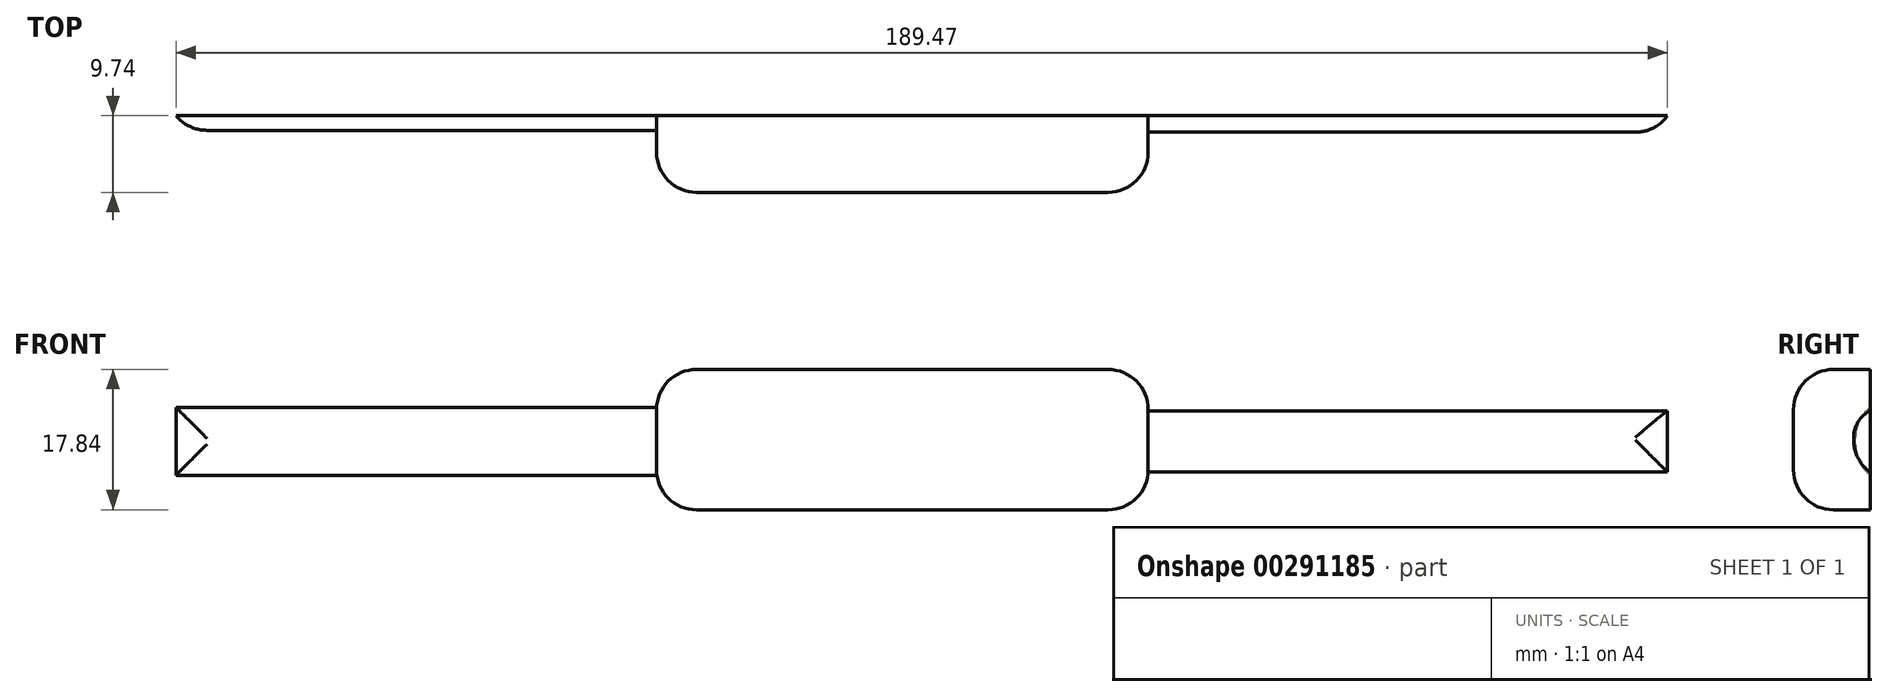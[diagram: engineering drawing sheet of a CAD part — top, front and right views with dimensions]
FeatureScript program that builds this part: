
annotation { "Feature Type Name" : "Feature", "Feature Type Description" : "" }
export const myFeature = defineFeature(function(context is Context, id is Id, definition is map)
    precondition{}
    {
        {
            var Q0;
            Q0=qCreatedBy(makeId("Front.planeOp"),FACE);
            var sketch = newSketch(context, id + "F0", { "sketchPlane" : qUnion([Q0])});
            skLineSegment(sketch, "E0.bottom", {"start": v(0, 0) * mm, "end": v(62.44, 0) * mm});
            skLineSegment(sketch, "E0.top", {"start": v(0, 17.84) * mm, "end": v(62.44, 17.84) * mm});
            skLineSegment(sketch, "E0.left", {"start": v(0, 0) * mm, "end": v(0, 17.84) * mm});
            skLineSegment(sketch, "E0.right", {"start": v(62.44, 0) * mm, "end": v(62.44, 17.84) * mm});
            skSolve(sketch);
        }
        {
            var Q0;
            Q0=makeQuery(id+"F0.imprint","IMPRINT",FACE,{"disambiguationData":[TD([[makeQuery(id+"F0.imprint","IMPRINT",EDGE,{"derivedFrom":sQuery(id+"F0.wireOp",EDGE,"E0.bottom")}),1.0]])]});
            var Q1;
            Q1 = qSketchRegion(id + "F0", true);
            extrude(context, id + "F1", {"entities" : qUnion([Q0, Q1]), "depth" : 9.74 * mm});
        }
        {
            var Q0;
            Q0=makeQuery(id+"F1.opExtrude","CAP_EDGE",EDGE,{"disambiguationData":[OSD([sQuery(id+"F0.wireOp",EDGE,"E0.top")])],"isStart":false});
            var Q1;
            Q1=makeQuery(id+"F1.opExtrude","CAP_EDGE",EDGE,{"disambiguationData":[OSD([sQuery(id+"F0.wireOp",EDGE,"E0.bottom")])],"isStart":false});
            fillet(context, id + "F2", {"entities" : qUnion([Q0, Q1]), "radius" : 5.08 * mm, "tangentPropagation" : true, "allowEdgeOverflow" : false});
        }
        {
            var Q0;
            Q0=makeQuery(id+"F1.opExtrude","CAP_EDGE",EDGE,{"disambiguationData":[OSD([sQuery(id+"F0.wireOp",EDGE,"E0.right")])],"isStart":false});
            var Q1;
            Q1=makeQuery(id+"F1.opExtrude","CAP_EDGE",EDGE,{"disambiguationData":[OSD([sQuery(id+"F0.wireOp",EDGE,"E0.left")])],"isStart":false});
            fillet(context, id + "F3", {"entities" : qUnion([Q0, Q1]), "radius" : 5.08 * mm, "tangentPropagation" : true, "allowEdgeOverflow" : false});
        }
        {
            var Q0;
            Q0=qCreatedBy(makeId("Front.planeOp"),FACE);
            var sketch = newSketch(context, id + "F4", { "sketchPlane" : qUnion([Q0])});
            skLineSegment(sketch, "E1.bottom", {"start": v(59.95, 12.57) * mm, "end": v(128.43, 12.57) * mm});
            skLineSegment(sketch, "E1.top", {"start": v(59.95, 4.79) * mm, "end": v(128.43, 4.79) * mm});
            skLineSegment(sketch, "E1.left", {"start": v(59.95, 12.57) * mm, "end": v(59.95, 4.79) * mm});
            skLineSegment(sketch, "E1.right", {"start": v(128.43, 12.57) * mm, "end": v(128.43, 4.79) * mm});
            skSolve(sketch);
        }
        {
            var Q0;
            Q0=makeQuery(id+"F4.imprint","IMPRINT",FACE,{"disambiguationData":[TD([[makeQuery(id+"F4.imprint","IMPRINT",EDGE,{"derivedFrom":sQuery(id+"F4.wireOp",EDGE,"E1.bottom")}),-1.0]])]});
            extrude(context, id + "F5", {"entities" : qUnion([Q0]), "operationType" : NewBodyOperationType.ADD, "depth" : 2.1 * mm});
        }
        {
            var Q0;
            Q0=qCreatedBy(makeId("Front.planeOp"),FACE);
            var sketch = newSketch(context, id + "F6", { "sketchPlane" : qUnion([Q0])});
            skLineSegment(sketch, "E2.bottom", {"start": v(0, 13.03) * mm, "end": v(-61.04, 13.03) * mm});
            skLineSegment(sketch, "E2.top", {"start": v(0, 4.4) * mm, "end": v(-61.04, 4.4) * mm});
            skLineSegment(sketch, "E2.left", {"start": v(0, 13.03) * mm, "end": v(0, 4.4) * mm});
            skLineSegment(sketch, "E2.right", {"start": v(-61.04, 13.03) * mm, "end": v(-61.04, 4.4) * mm});
            skSolve(sketch);
        }
        {
            var Q0;
            Q0=makeQuery(id+"F6.imprint","IMPRINT",FACE,{"disambiguationData":[TD([[makeQuery(id+"F6.imprint","IMPRINT",EDGE,{"derivedFrom":sQuery(id+"F6.wireOp",EDGE,"E2.bottom")}),1.0]])]});
            extrude(context, id + "F7", {"entities" : qUnion([Q0]), "operationType" : NewBodyOperationType.ADD, "depth" : 1.86 * mm});
        }
        {
            var Q0;
            Q0=makeQuery(id+"F7.opExtrude","CAP_EDGE",EDGE,{"disambiguationData":[OSD([sQuery(id+"F6.wireOp",EDGE,"E2.bottom")])],"isStart":false});
            var Q1;
            Q1=makeQuery(id+"F7.opExtrude","CAP_EDGE",EDGE,{"disambiguationData":[OSD([sQuery(id+"F6.wireOp",EDGE,"E2.right")])],"isStart":false});
            fillet(context, id + "F8", {"entities" : qUnion([Q0, Q1]), "radius" : 5.08 * mm, "tangentPropagation" : true, "allowEdgeOverflow" : false});
        }
        {
            var Q0;
            Q0=makeQuery(id+"F7.opExtrude","CAP_EDGE",EDGE,{"disambiguationData":[OSD([sQuery(id+"F6.wireOp",EDGE,"E2.top")])],"isStart":false});
            fillet(context, id + "F9", {"entities" : qUnion([Q0]), "radius" : 5.08 * mm, "tangentPropagation" : true, "allowEdgeOverflow" : false});
        }
        {
            var Q0;
            Q0=makeQuery(id+"F5.opExtrude","CAP_EDGE",EDGE,{"disambiguationData":[OSD([sQuery(id+"F4.wireOp",EDGE,"E1.top")])],"isStart":false});
            var Q1;
            Q1=makeQuery(id+"F5.opExtrude","CAP_EDGE",EDGE,{"disambiguationData":[OSD([sQuery(id+"F4.wireOp",EDGE,"E1.right")])],"isStart":false});
            fillet(context, id + "F10", {"entities" : qUnion([Q0, Q1]), "radius" : 5.08 * mm, "tangentPropagation" : true, "allowEdgeOverflow" : false});
        }
        {
            var Q0;
            Q0=makeQuery(id+"F5.opExtrude","CAP_EDGE",EDGE,{"disambiguationData":[OSD([sQuery(id+"F4.wireOp",EDGE,"E1.bottom")])],"isStart":false});
            fillet(context, id + "F11", {"entities" : qUnion([Q0]), "radius" : 3.76 * mm, "tangentPropagation" : true, "allowEdgeOverflow" : false});
        }
    });
